# Revit family: Haworth_XSeries_Locker_Single
name_source: partatom
category: Furniture Systems
revit_build: Autodesk Revit 2018 (Build: 20170223_1515(x64)
units: mm (PartAtom-declared; Revit-internal decimal feet)

## family parameters
Always vertical = Yes
Cut with Voids When Loaded = No
OmniClass Number = 23.40.70.14.64.21
OmniClass Title = Systems Furniture
Part Type = Normal
Room Calculation Point = No
Round Connector Dimension = Use Diameter
Shared = No
Work Plane-Based = No

## types (4) — shared parameters
Actual Height = 51 1/2"
Assembly Code = E2020200
Base Height = 1 7/8"
Classic Pull = No
Crescent Pull = No
Custom Depth = No
Custom Height = No
Custom Size = No
Custom Width = No
Description = Haworth XSeries Locker - Single
Door Height = 48 1/4"
Height = 51 1/2"
J Pull = No
Linear Pull = Yes
Manufacturer = Haworth
Max. Depth = 23 3/4"
Max. Height = 64 1/2"
Max. Width = 18"
Min. Depth = 18 3/4"
Min. Height = 39 1/2"
Min. Width = 12"
Model = JA18
Panel Thickness = 3/4"
Pull Ellipse = No
Pull Finish = Haworth _ Metal _ Brushed Aluminum
Pull Height = 24 1/8"
Radius Pull = No
Revision Number = 3
Size = Verify Final Dim. w/ Haworth
Standard Depths = 18.75, 23.75 in.
Standard Heights = 39.5, 40.5, 48.5, 51.5, 56.5, 63.5, 64.5 in.
Standard Widths = 12, 18 in.
Sustainability Info = https://www.haworth.com
Taper Pull = No
Top Height = 1 1/4"
URL = http://www.haworth.com
URL - Product = https://www.haworth.com
Warranty = http://www.haworth.com

## per-type parameters (varying)
| type | Actual Depth | Actual Width | Depth | Door Width | Pull Offset Centerline | Width |
| 18d 12w 51h | 18 3/4" | 12" | 18 3/4" | 11 7/8" | 10 1/2" | 12" |
| 18d 18w 51h | 18 3/4" | 18" | 18 3/4" | 17 7/8" | 16 1/2" | 18" |
| 24d 12w 51h | 23 3/4" | 12" | 23 3/4" | 11 7/8" | 10 1/2" | 12" |
| 24d 18w 51h | 23 3/4" | 18" | 23 3/4" | 17 7/8" | 16 1/2" | 18" |

## geometry (parser evidence)
native form markers: Sweep x8
no freeform markers — native parametric forms only
